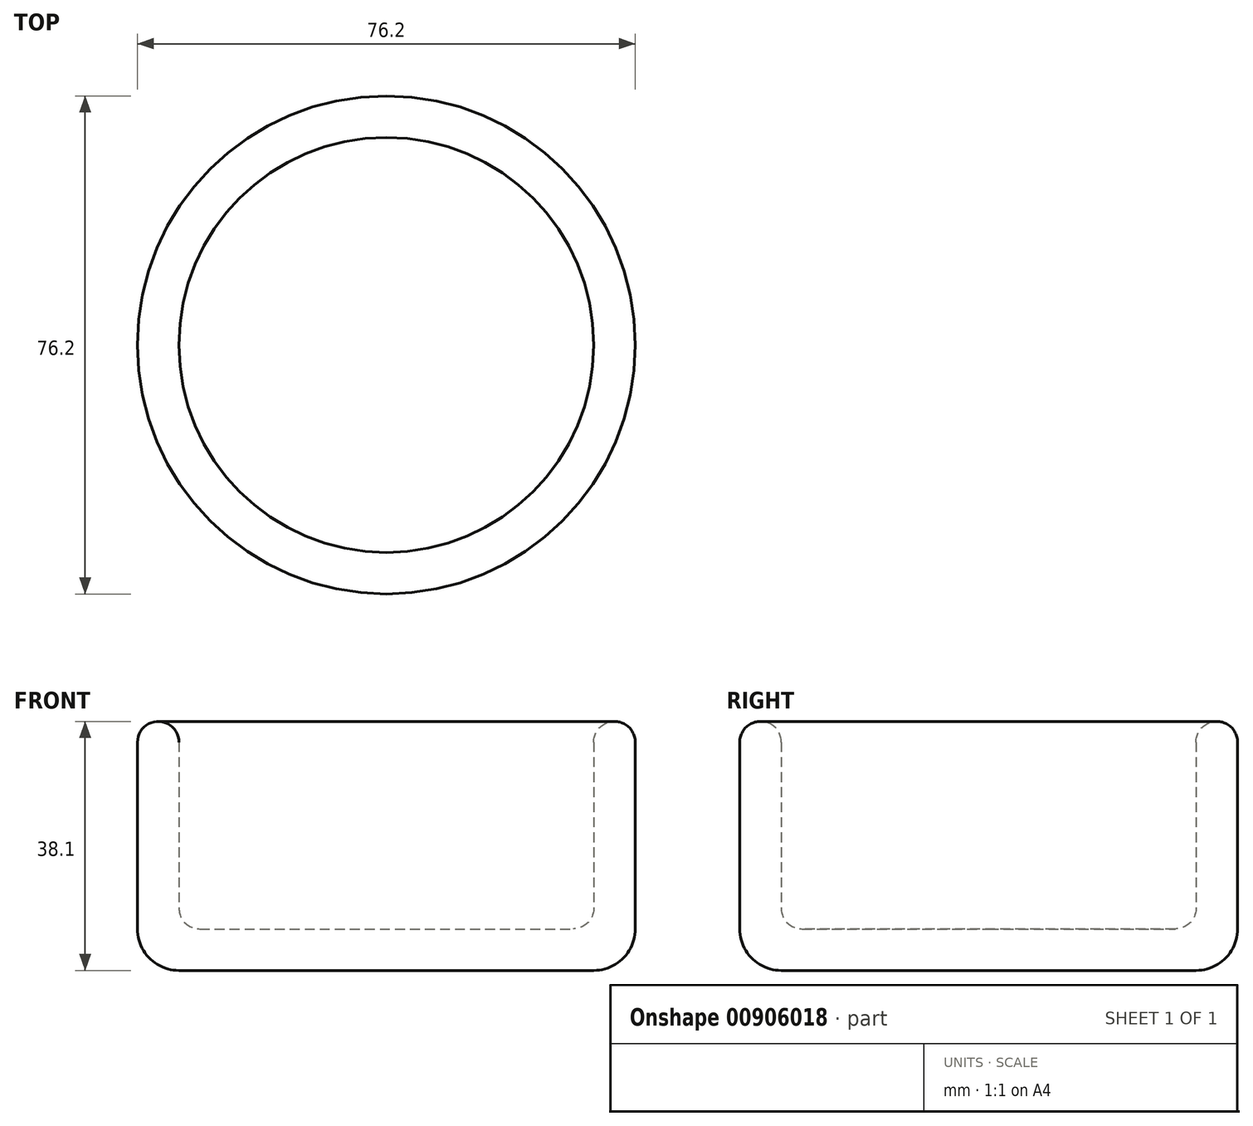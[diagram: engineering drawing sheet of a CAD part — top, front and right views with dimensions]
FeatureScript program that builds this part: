
annotation { "Feature Type Name" : "Feature", "Feature Type Description" : "" }
export const myFeature = defineFeature(function(context is Context, id is Id, definition is map)
    precondition{}
    {
        {
            var Q0;
            Q0=qCreatedBy(makeId("Right.planeOp"),FACE);
            var sketch = newSketch(context, id + "F0", { "sketchPlane" : qUnion([Q0])});
            skLineSegment(sketch, "E0", {"start": v(0, 0) * mm, "end": v(-31.75, 0) * mm});
            skLineSegment(sketch, "E1", {"start": v(-38.1, 6.35) * mm, "end": v(-38.1, 34.93) * mm});
            skLineSegment(sketch, "E2", {"start": v(-34.93, 38.1) * mm, "end": v(-34.92, 38.1) * mm});
            skLineSegment(sketch, "E3", {"start": v(-31.75, 34.93) * mm, "end": v(-31.75, 9.52) * mm});
            skLineSegment(sketch, "E4", {"start": v(-28.57, 6.35) * mm, "end": v(0, 6.35) * mm});
            skLineSegment(sketch, "E5", {"start": v(0, 6.35) * mm, "end": v(0, 0) * mm});
            skPoint(sketch, "E6.visualSharp", {"position": v(-38.1, 0) * mm});
            skArc(sketch, "E6.filletArc", {"start": v(-38.1, 6.35) * mm, "mid": v(-36.24, 1.86) * mm, "end": v(-31.75, 0) * mm});
            skPoint(sketch, "E7.visualSharp", {"position": v(-31.75, 38.1) * mm});
            skArc(sketch, "E7.filletArc", {"start": v(-31.75, 34.93) * mm, "mid": v(-32.68, 37.17) * mm, "end": v(-34.92, 38.1) * mm});
            skPoint(sketch, "E8.visualSharp", {"position": v(-38.1, 38.1) * mm});
            skArc(sketch, "E8.filletArc", {"start": v(-34.93, 38.1) * mm, "mid": v(-37.17, 37.17) * mm, "end": v(-38.1, 34.93) * mm});
            skArc(sketch, "E9.filletArc", {"start": v(-31.75, 9.52) * mm, "mid": v(-30.82, 7.28) * mm, "end": v(-28.57, 6.35) * mm});
            skLineSegment(sketch, "E10", {"start": v(0, 0) * mm, "end": v(0, 38.1) * mm, "construction": true});
            skPoint(sketch, "E10.endSnap0", {"position": v(0, 3.18) * mm});
            skSolve(sketch);
        }
        {
            var Q0;
            Q0 = qSketchRegion(id + "F0", true);
            var Q1;
            Q1=sQuery(id+"F0.wireOp",EDGE,"E10");
            revolve(context, id + "F1", {"surfaceOperationType" : NewSurfaceOperationType.NEW, "entities" : qUnion([Q0]), "axis" : qUnion([Q1]), "revolveType" : RevolveType.FULL});
        }
    });
